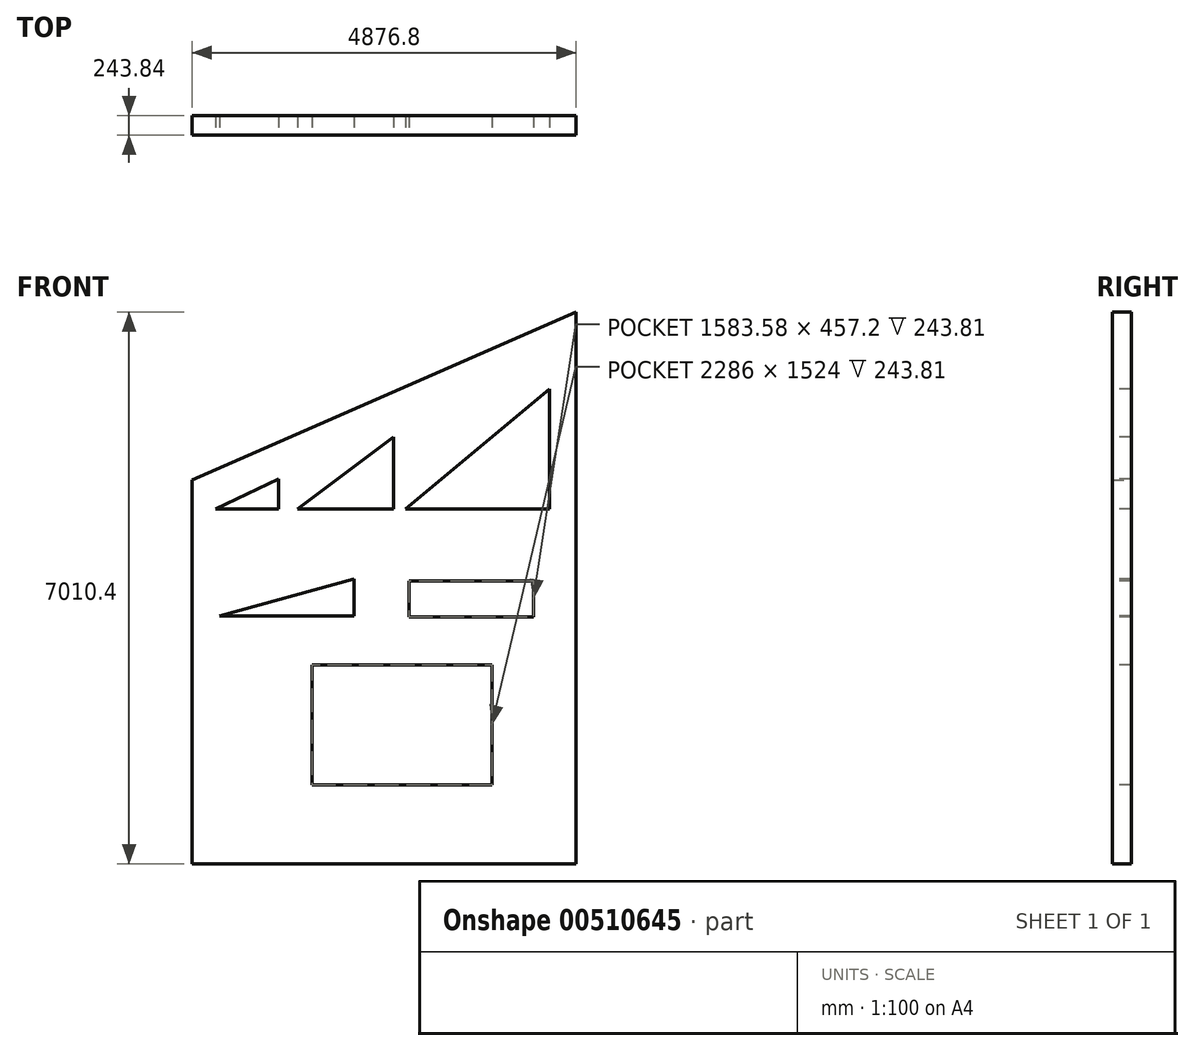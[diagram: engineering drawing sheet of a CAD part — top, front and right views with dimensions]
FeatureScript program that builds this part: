
annotation { "Feature Type Name" : "Feature", "Feature Type Description" : "" }
export const myFeature = defineFeature(function(context is Context, id is Id, definition is map)
    precondition{}
    {
        {
            var Q0;
            Q0=qCreatedBy(makeId("Front.planeOp"),FACE);
            var sketch = newSketch(context, id + "F0", { "sketchPlane" : qUnion([Q0])});
            skLineSegment(sketch, "E0", {"start": v(-2309.46, 369.32) * mm, "end": v(-2309.46, -4507.48) * mm});
            skLineSegment(sketch, "E1", {"start": v(-2309.46, -4507.48) * mm, "end": v(2567.34, -4507.48) * mm});
            skLineSegment(sketch, "E2", {"start": v(2567.34, -4507.48) * mm, "end": v(2567.34, 2502.92) * mm});
            skLineSegment(sketch, "E3", {"start": v(2567.34, 2502.92) * mm, "end": v(-2309.46, 369.32) * mm});
            skSolve(sketch);
        }
        {
            var Q0;
            Q0 = qSketchRegion(id + "F0", true);
            extrude(context, id + "F1", {"entities" : qUnion([Q0]), "depth" : 243.84 * mm, "offsetDistance" : 30.48 * mm});
        }
        {
            var Q0;
            Q0=makeQuery(id+"F1.opExtrude","CAP_FACE",FACE,{"disambiguationData":[OSD([sQuery(id+"F0.wireOp",EDGE,"E0"),sQuery(id+"F0.wireOp",EDGE,"E1"),sQuery(id+"F0.wireOp",EDGE,"E2"),sQuery(id+"F0.wireOp",EDGE,"E3")])],"isStart":false});
            var sketch = newSketch(context, id + "F2", { "sketchPlane" : qUnion([Q0])});
            skLineSegment(sketch, "E4", {"start": v(2230.93, 1524) * mm, "end": v(2230.93, 0) * mm});
            skLineSegment(sketch, "E5", {"start": v(2230.93, 0) * mm, "end": v(402.13, 0) * mm});
            skLineSegment(sketch, "E6", {"start": v(402.13, 0) * mm, "end": v(2230.93, 1524) * mm});
            skLineSegment(sketch, "E7", {"start": v(250.86, 914.4) * mm, "end": v(250.86, 0) * mm});
            skLineSegment(sketch, "E8", {"start": v(250.86, 0) * mm, "end": v(-968.34, 0) * mm});
            skLineSegment(sketch, "E9", {"start": v(-968.34, 0) * mm, "end": v(250.86, 914.4) * mm});
            skLineSegment(sketch, "E10", {"start": v(-1212.34, 382.38) * mm, "end": v(-1212.34, 0) * mm});
            skPoint(sketch, "E10.endSnap0", {"position": v(-358.74, 0) * mm});
            skLineSegment(sketch, "E11", {"start": v(-1212.34, 0) * mm, "end": v(-2011.31, 0) * mm});
            skLineSegment(sketch, "E12", {"start": v(-2011.31, 0) * mm, "end": v(-1212.34, 382.38) * mm});
            skLineSegment(sketch, "E13", {"start": v(-785.46, -1980.56) * mm, "end": v(-785.46, -3504.56) * mm});
            skLineSegment(sketch, "E14", {"start": v(-785.46, -3504.56) * mm, "end": v(1500.54, -3504.56) * mm});
            skLineSegment(sketch, "E15", {"start": v(1500.54, -3504.56) * mm, "end": v(1500.54, -1980.56) * mm});
            skLineSegment(sketch, "E16", {"start": v(1500.54, -1980.56) * mm, "end": v(-785.46, -1980.56) * mm});
            skLineSegment(sketch, "E17.bottom", {"start": v(446.63, -913.76) * mm, "end": v(2030.21, -913.76) * mm});
            skLineSegment(sketch, "E17.top", {"start": v(446.63, -1370.96) * mm, "end": v(2030.21, -1370.96) * mm});
            skLineSegment(sketch, "E17.left", {"start": v(446.63, -913.76) * mm, "end": v(446.63, -1370.96) * mm});
            skLineSegment(sketch, "E17.right", {"start": v(2030.21, -913.76) * mm, "end": v(2030.21, -1370.96) * mm});
            skLineSegment(sketch, "E18", {"start": v(-252.33, -888.43) * mm, "end": v(-252.33, -1358.05) * mm});
            skLineSegment(sketch, "E19", {"start": v(-252.33, -1358.05) * mm, "end": v(-1956.04, -1358.05) * mm});
            skLineSegment(sketch, "E20", {"start": v(-1956.04, -1358.05) * mm, "end": v(-252.33, -888.43) * mm});
            skSolve(sketch);
        }
        {
            var Q0;
            Q0 = qSketchRegion(id + "F2", true);
            extrude(context, id + "F3", {"entities" : qUnion([Q0]), "operationType" : NewBodyOperationType.REMOVE, "oppositeDirection" : true, "depth" : 243.8 * mm, "offsetDistance" : 30.48 * mm});
        }
    });
